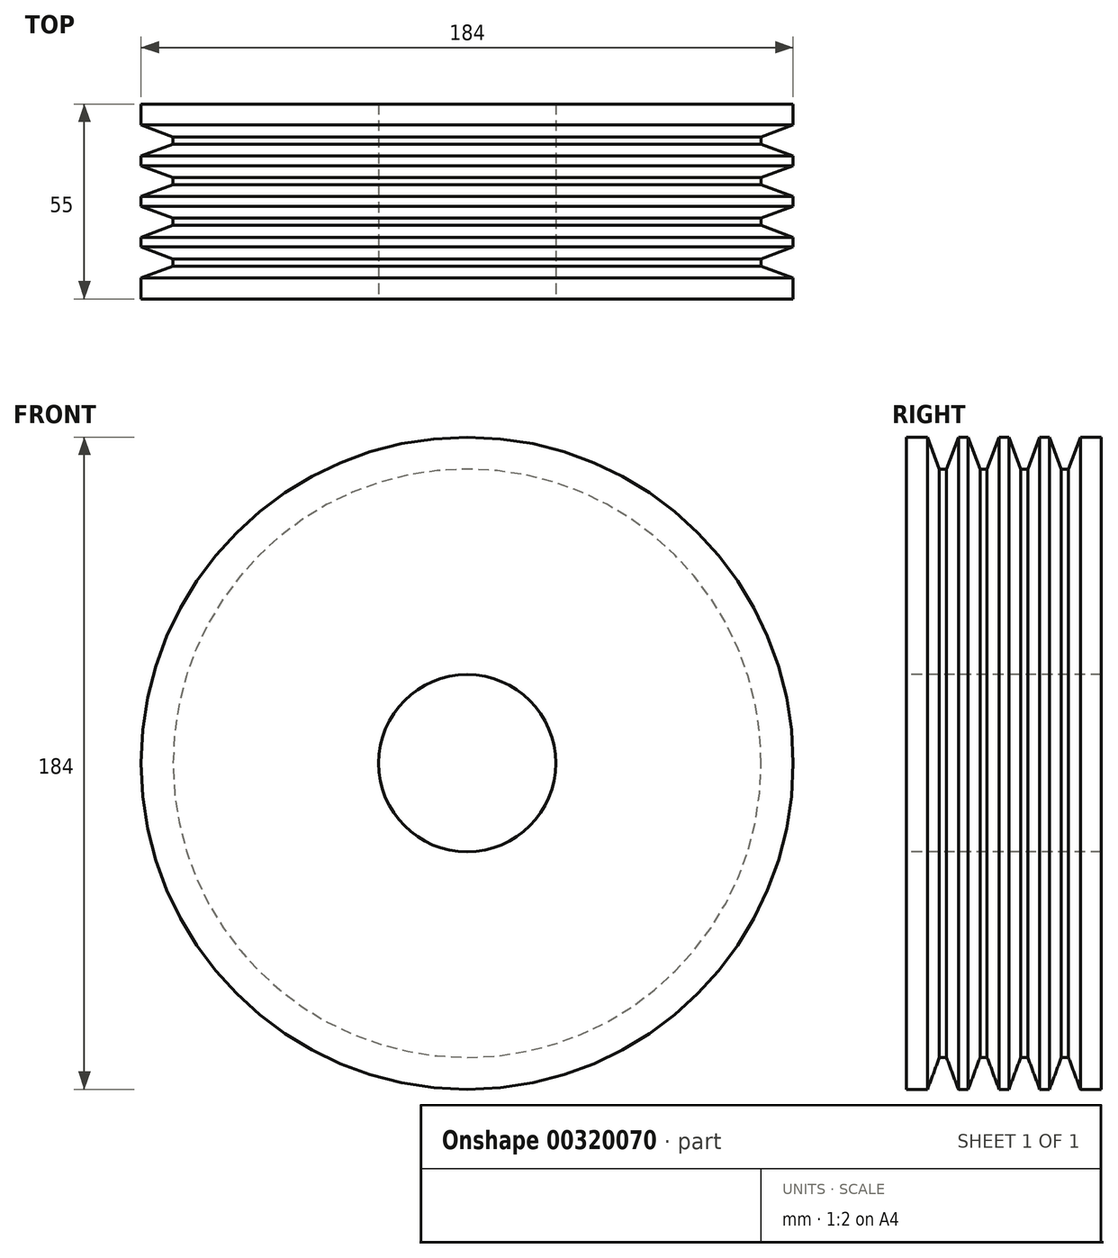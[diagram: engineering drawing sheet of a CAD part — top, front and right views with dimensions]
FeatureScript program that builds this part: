
annotation { "Feature Type Name" : "Feature", "Feature Type Description" : "" }
export const myFeature = defineFeature(function(context is Context, id is Id, definition is map)
    precondition{}
    {
        {
            var Q0;
            Q0=qCreatedBy(makeId("Right.planeOp"),FACE);
            var sketch = newSketch(context, id + "F0", { "sketchPlane" : qUnion([Q0])});
            skLineSegment(sketch, "E0", {"start": v(0, 0) * mm, "end": v(0, 92) * mm});
            skLineSegment(sketch, "E1", {"start": v(0, 92) * mm, "end": v(5.94, 92) * mm});
            skLineSegment(sketch, "E2", {"start": v(5.94, 92) * mm, "end": v(9.29, 83) * mm});
            skLineSegment(sketch, "E3", {"start": v(9.29, 83) * mm, "end": v(11.29, 83) * mm});
            skLineSegment(sketch, "E4", {"start": v(11.29, 83) * mm, "end": v(14.64, 92) * mm});
            skLineSegment(sketch, "E5", {"start": v(14.64, 92) * mm, "end": v(17.41, 92) * mm});
            skLineSegment(sketch, "E6", {"start": v(17.41, 92) * mm, "end": v(20.76, 83) * mm});
            skLineSegment(sketch, "E7", {"start": v(20.76, 83) * mm, "end": v(22.76, 83) * mm});
            skLineSegment(sketch, "E8", {"start": v(22.76, 83) * mm, "end": v(26.11, 92) * mm});
            skLineSegment(sketch, "E9", {"start": v(26.11, 92) * mm, "end": v(28.89, 92) * mm});
            skLineSegment(sketch, "E10", {"start": v(28.89, 92) * mm, "end": v(32.24, 83) * mm});
            skLineSegment(sketch, "E11", {"start": v(32.24, 83) * mm, "end": v(34.24, 83) * mm});
            skLineSegment(sketch, "E12", {"start": v(34.24, 83) * mm, "end": v(37.59, 92) * mm});
            skLineSegment(sketch, "E13", {"start": v(37.59, 92) * mm, "end": v(40.36, 92) * mm});
            skLineSegment(sketch, "E14", {"start": v(40.36, 92) * mm, "end": v(43.71, 83) * mm});
            skLineSegment(sketch, "E15", {"start": v(43.71, 83) * mm, "end": v(45.71, 83) * mm});
            skLineSegment(sketch, "E16", {"start": v(45.71, 83) * mm, "end": v(49.06, 92) * mm});
            skLineSegment(sketch, "E17", {"start": v(49.06, 92) * mm, "end": v(55, 92) * mm});
            skLineSegment(sketch, "E18", {"start": v(55, 92) * mm, "end": v(55, 0) * mm});
            skLineSegment(sketch, "E19", {"start": v(0, 0) * mm, "end": v(55, 0) * mm});
            skLineSegment(sketch, "E20", {"start": v(10.29, 83) * mm, "end": v(10.29, 92) * mm, "construction": true});
            skLineSegment(sketch, "E21", {"start": v(5.94, 92) * mm, "end": v(14.64, 92) * mm, "construction": true});
            skSolve(sketch);
        }
        {
            var Q0;
            Q0=makeQuery(id+"F0.imprint","IMPRINT",FACE,{"disambiguationData":[TD([[makeQuery(id+"F0.imprint","IMPRINT",EDGE,{"derivedFrom":sQuery(id+"F0.wireOp",EDGE,"E0")}),-1.0]])]});
            var Q1;
            Q1=sQuery(id+"F0.wireOp",EDGE,"E19");
            revolve(context, id + "F1", {"entities" : qUnion([Q0]), "axis" : qUnion([Q1]), "revolveType" : RevolveType.FULL});
        }
        {
            var Q0;
            Q0=makeQuery(id+"F1.opRevolve","SWEPT_FACE",FACE,{"disambiguationData":[OSD([sQuery(id+"F0.wireOp",EDGE,"E0")])]});
            var sketch = newSketch(context, id + "F2", { "sketchPlane" : qUnion([Q0])});
            skCircle(sketch, "E22", {"center": v(0, 0) * mm, "radius": 25 * mm});
            skSolve(sketch);
        }
        {
            var Q0;
            Q0 = qSketchRegion(id + "F2", true);
            extrude(context, id + "F3", {"entities" : qUnion([Q0]), "operationType" : NewBodyOperationType.REMOVE, "endBound" : BoundingType.THROUGH_ALL, "oppositeDirection" : true, "depth" : 25 * mm});
        }
    });
